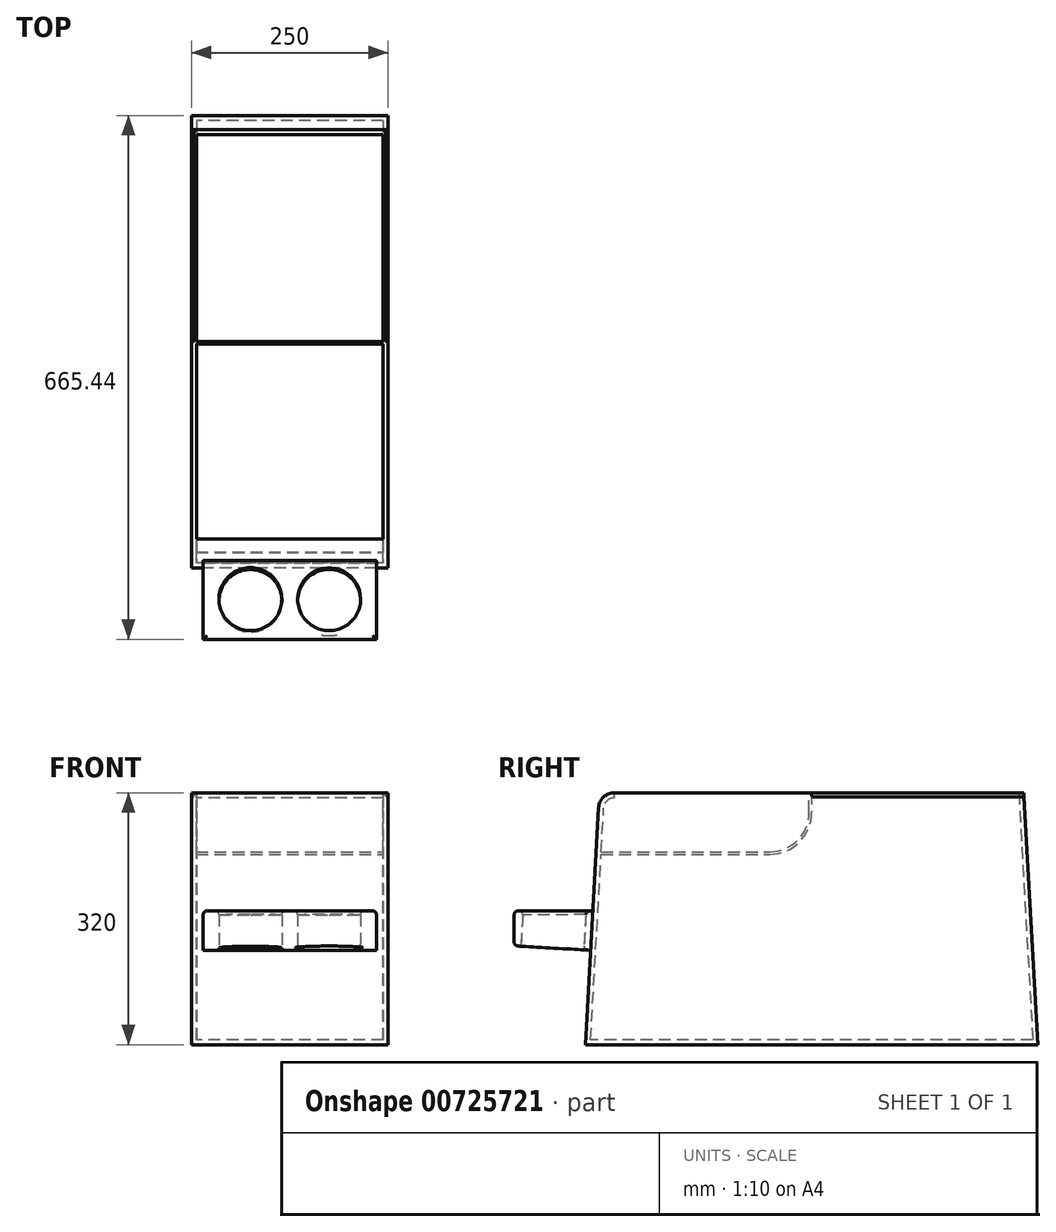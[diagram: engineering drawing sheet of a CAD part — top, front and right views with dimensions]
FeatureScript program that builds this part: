
annotation { "Feature Type Name" : "Feature", "Feature Type Description" : "" }
export const myFeature = defineFeature(function(context is Context, id is Id, definition is map)
    precondition{}
    {
        {
            var Q0;
            Q0=qCreatedBy(makeId("Right.planeOp"),FACE);
            var sketch = newSketch(context, id + "F0", { "sketchPlane" : qUnion([Q0])});
            skLineSegment(sketch, "E0.bottom", {"start": v(287.5, 160) * mm, "end": v(-287.5, 160) * mm});
            skLineSegment(sketch, "E0.top", {"start": v(287.5, -160) * mm, "end": v(-287.5, -160) * mm});
            skLineSegment(sketch, "E0.left", {"start": v(287.5, 160) * mm, "end": v(287.5, -160) * mm});
            skLineSegment(sketch, "E0.right", {"start": v(-287.5, 160) * mm, "end": v(-287.5, -160) * mm});
            skPoint(sketch, "E0.middle", {"position": v(0, 0) * mm});
            skLineSegment(sketch, "E1", {"start": v(-287.5, -160) * mm, "end": v(-270.56, 141.12) * mm});
            skLineSegment(sketch, "E2", {"start": v(-250.6, 160) * mm, "end": v(250.6, 160) * mm});
            skLineSegment(sketch, "E3", {"start": v(269.5, 160) * mm, "end": v(287.5, -160) * mm});
            skPoint(sketch, "E4.visualSharp", {"position": v(-269.5, 160) * mm});
            skArc(sketch, "E4.filletArc", {"start": v(-250.6, 160) * mm, "mid": v(-264.33, 154.53) * mm, "end": v(-270.56, 141.12) * mm});
            skPoint(sketch, "E5.visualSharp", {"position": v(269.5, 160) * mm});
            skSolve(sketch);
        }
        {
            var Q0;
            Q0=makeQuery(id+"F0.imprint","IMPRINT",FACE,{"disambiguationData":[TD([[makeQuery(id+"F0.imprint","IMPRINT",EDGE,{"derivedFrom":sQuery(id+"F0.wireOp",EDGE,"E0.top")}),-1.0]])]});
            extrude(context, id + "F1", {"entities" : qUnion([Q0]), "depth" : 250 * mm, "offsetDistance" : 25 * mm});
        }
        {
            var Q0;
            Q0=makeQuery(id+"F1.opExtrude","SWEPT_FACE",FACE,{"disambiguationData":[OSD([sQuery(id+"F0.wireOp",EDGE,"E0.bottom")])]});
            var Q1;
            Q1=makeQuery(id+"F1.opExtrude","SWEPT_FACE",FACE,{"disambiguationData":[OSD([sQuery(id+"F0.wireOp",EDGE,"E5.filletArc")])]});
            shell(context, id + "F2", {"entities" : qUnion([Q0, Q1]), "thickness" : 6.35 * mm});
        }
        {
            var Q0;
            Q0=makeQuery(id+"F1.opExtrude","CAP_FACE",FACE,{"disambiguationData":[OSD([sQuery(id+"F0.wireOp",EDGE,"E0.bottom"),sQuery(id+"F0.wireOp",EDGE,"E0.top"),sQuery(id+"F0.wireOp",EDGE,"E1"),sQuery(id+"F0.wireOp",EDGE,"E3"),sQuery(id+"F0.wireOp",EDGE,"E4.filletArc")])],"isStart":false});
            var sketch = newSketch(context, id + "F3", { "sketchPlane" : qUnion([Q0])});
            skLineSegment(sketch, "E6", {"start": v(-273.72, 85) * mm, "end": v(-53.17, 85) * mm});
            skLineSegment(sketch, "E7", {"start": v(-273.9, 81.82) * mm, "end": v(-53.17, 81.82) * mm});
            skLineSegment(sketch, "E8", {"start": v(0, 160) * mm, "end": v(0, 135) * mm});
            skLineSegment(sketch, "E9", {"start": v(-53.17, 85) * mm, "end": v(-53.17, 85) * mm});
            skLineSegment(sketch, "E10", {"start": v(-3.17, 135) * mm, "end": v(-3.18, 160) * mm});
            skLineSegment(sketch, "E11", {"start": v(-53.17, 81.82) * mm, "end": v(-53.17, 81.82) * mm});
            skPoint(sketch, "E12.visualSharp", {"position": v(-3.17, 85) * mm});
            skArc(sketch, "E12.filletArc", {"start": v(-53.17, 85) * mm, "mid": v(-17.82, 99.64) * mm, "end": v(-3.17, 135) * mm});
            skPoint(sketch, "E13.visualSharp", {"position": v(0, 81.82) * mm});
            skArc(sketch, "E13.filletArc", {"start": v(-53.17, 81.83) * mm, "mid": v(-15.57, 97.4) * mm, "end": v(0, 135) * mm});
            skSolve(sketch);
        }
        {
            var Q0;
            {var subQ1=sQuery(id+"F3.wireOp",EDGE,"E6");Q0=makeQuery(id+"F3.imprint","IMPRINT",FACE,{"disambiguationData":[TD([[makeQuery(id+"F3.imprint","IMPRINT",EDGE,{"derivedFrom":subQ1}),-1.0]])]});}
            extrude(context, id + "F4", {"entities" : qUnion([Q0]), "operationType" : NewBodyOperationType.ADD, "oppositeDirection" : true, "depth" : 250 * mm, "offsetDistance" : 25 * mm});
        }
        {
            var Q0;
            {var subQ0=sQuery(id+"F0.wireOp",EDGE,"E0.bottom");Q0=makeQuery(id+"F4.boolean.opBoolean","MERGE",FACE,{"derivedFrom":[makeQuery(id+"F1.opExtrude","SWEPT_FACE",FACE,{"disambiguationData":[OSD([subQ0])]}),makeQuery(id+"F4.opExtrude","SWEPT_FACE",FACE,{"disambiguationData":[OSD([subQ0])]})]});}
            var sketch = newSketch(context, id + "F5", { "sketchPlane" : qUnion([Q0])});
            skLineSegment(sketch, "E14.bottom", {"start": v(0, 269.5) * mm, "end": v(3.17, 269.5) * mm});
            skLineSegment(sketch, "E14.top", {"start": v(0, 0) * mm, "end": v(3.18, 0) * mm});
            skLineSegment(sketch, "E14.left", {"start": v(0, 269.5) * mm, "end": v(0, 0) * mm});
            skLineSegment(sketch, "E14.right", {"start": v(3.17, 269.5) * mm, "end": v(3.18, 0) * mm});
            skLineSegment(sketch, "E15.bottom", {"start": v(250, 269.5) * mm, "end": v(246.82, 269.5) * mm});
            skLineSegment(sketch, "E15.top", {"start": v(250, 0) * mm, "end": v(246.83, 0) * mm});
            skLineSegment(sketch, "E15.left", {"start": v(250, 269.5) * mm, "end": v(250, 0) * mm});
            skLineSegment(sketch, "E15.right", {"start": v(246.82, 269.5) * mm, "end": v(246.83, 0) * mm});
            skSolve(sketch);
        }
        {
            var Q0;
            Q0=makeQuery(id+"F5.imprint","IMPRINT",FACE,{"disambiguationData":[TD([[makeQuery(id+"F5.imprint","IMPRINT",EDGE,{"derivedFrom":sQuery(id+"F5.wireOp",EDGE,"E14.bottom")}),1.0]])]});
            var Q1;
            Q1=makeQuery(id+"F5.imprint","IMPRINT",FACE,{"disambiguationData":[TD([[makeQuery(id+"F5.imprint","IMPRINT",EDGE,{"derivedFrom":sQuery(id+"F5.wireOp",EDGE,"E15.bottom")}),1.0]])]});
            extrude(context, id + "F6", {"entities" : qUnion([Q0, Q1]), "operationType" : NewBodyOperationType.REMOVE, "oppositeDirection" : true, "depth" : 5 * mm, "offsetDistance" : 25 * mm});
        }
        {
            var Q0;
            Q0=makeQuery(id+"F6.boolean.opBoolean","COPY",FACE,{"derivedFrom":makeQuery(id+"F6.opExtrude","SWEPT_FACE",FACE,{"disambiguationData":[OSD([sQuery(id+"F5.wireOp",EDGE,"E14.bottom")])]})});
            var Q1;
            Q1=makeQuery(id+"F6.boolean.opBoolean","COPY",FACE,{"derivedFrom":makeQuery(id+"F6.opExtrude","SWEPT_FACE",FACE,{"disambiguationData":[OSD([sQuery(id+"F5.wireOp",EDGE,"E15.bottom")])]})});
            extrude(context, id + "F7", {"entities" : qUnion([Q0, Q1]), "operationType" : NewBodyOperationType.REMOVE, "oppositeDirection" : true, "depth" : 25 * mm, "offsetDistance" : 25 * mm});
        }
        {
            var Q0;
            {var subQ0=sQuery(id+"F5.wireOp",EDGE,"E14.right");var subQ1=sQuery(id+"F5.wireOp",EDGE,"E14.bottom");var subQ2=sQuery(id+"F0.wireOp",EDGE,"E3");var subQ3=sQuery(id+"F0.wireOp",EDGE,"E0.bottom");Q0=makeQuery(id+"F7.boolean.opBoolean","MERGE",EDGE,{"derivedFrom":[makeQuery(id+"F6.boolean.opBoolean","COPY",EDGE,{"derivedFrom":makeQuery(id+"F6.opExtrude","CAP_EDGE",EDGE,{"disambiguationData":[OSD([subQ0])],"isStart":false})})],"fromTools":[makeQuery(id+"F7.opExtrude","SWEPT_EDGE",EDGE,{"disambiguationData":[OSD([subQ3,subQ2,subQ1,subQ0]),TDD([makeQuery(id+"F6.boolean.opBoolean","COPY",VERTEX,{"derivedFrom":makeQuery(id+"F6.opExtrude","CAP_VERTEX",VERTEX,{"disambiguationData":[OSD([subQ3,subQ2,subQ1,subQ0])],"isStart":false})})])]})]});}
            var Q1;
            {var subQ0=sQuery(id+"F5.wireOp",EDGE,"E15.right");var subQ1=sQuery(id+"F5.wireOp",EDGE,"E15.bottom");var subQ2=sQuery(id+"F0.wireOp",EDGE,"E3");var subQ3=sQuery(id+"F0.wireOp",EDGE,"E0.bottom");Q1=makeQuery(id+"F7.boolean.opBoolean","MERGE",EDGE,{"derivedFrom":[makeQuery(id+"F6.boolean.opBoolean","COPY",EDGE,{"derivedFrom":makeQuery(id+"F6.opExtrude","CAP_EDGE",EDGE,{"disambiguationData":[OSD([subQ0])],"isStart":false})})],"fromTools":[makeQuery(id+"F7.opExtrude","SWEPT_EDGE",EDGE,{"disambiguationData":[OSD([subQ3,subQ2,subQ1,subQ0]),TDD([makeQuery(id+"F6.boolean.opBoolean","COPY",VERTEX,{"derivedFrom":makeQuery(id+"F6.opExtrude","CAP_VERTEX",VERTEX,{"disambiguationData":[OSD([subQ3,subQ2,subQ1,subQ0])],"isStart":false})})])]})]});}
            fillet(context, id + "F8", {"entities" : qUnion([Q0, Q1]), "radius" : 1.5 * mm, "tangentPropagation" : true, "allowEdgeOverflow" : false});
        }
        {
            var Q0;
            Q0=makeQuery(id+"F6.boolean.opBoolean","COPY",EDGE,{"derivedFrom":makeQuery(id+"F6.opExtrude","CAP_EDGE",EDGE,{"disambiguationData":[OSD([sQuery(id+"F5.wireOp",EDGE,"E14.top")])],"isStart":false})});
            var Q1;
            Q1=makeQuery(id+"F6.boolean.opBoolean","COPY",EDGE,{"derivedFrom":makeQuery(id+"F6.opExtrude","CAP_EDGE",EDGE,{"disambiguationData":[OSD([sQuery(id+"F5.wireOp",EDGE,"E15.top")])],"isStart":false})});
            fillet(context, id + "F9", {"entities" : qUnion([Q0, Q1]), "radius" : 1.5 * mm, "tangentPropagation" : true, "allowEdgeOverflow" : false});
        }
        {
            var Q0;
            Q0=makeQuery(id+"F1.opExtrude","CAP_FACE",FACE,{"disambiguationData":[OSD([sQuery(id+"F0.wireOp",EDGE,"E0.bottom"),sQuery(id+"F0.wireOp",EDGE,"E0.top"),sQuery(id+"F0.wireOp",EDGE,"E1"),sQuery(id+"F0.wireOp",EDGE,"E3"),sQuery(id+"F0.wireOp",EDGE,"E4.filletArc")])],"isStart":false});
            var sketch = newSketch(context, id + "F10", { "sketchPlane" : qUnion([Q0])});
            skLineSegment(sketch, "E16", {"start": v(-277.94, 10) * mm, "end": v(-280.75, -40) * mm});
            skLineSegment(sketch, "E17", {"start": v(-280.75, -40) * mm, "end": v(-377.94, -34.53) * mm});
            skLineSegment(sketch, "E18", {"start": v(-377.94, -34.53) * mm, "end": v(-377.94, 10) * mm});
            skLineSegment(sketch, "E19", {"start": v(-377.94, 10) * mm, "end": v(-277.94, 10) * mm});
            skSolve(sketch);
        }
        {
            var Q0;
            Q0=makeQuery(id+"F10.imprint","IMPRINT",FACE,{"disambiguationData":[TD([[makeQuery(id+"F10.imprint","IMPRINT",EDGE,{"derivedFrom":sQuery(id+"F10.wireOp",EDGE,"E16")}),1.0]])]});
            extrude(context, id + "F11", {"entities" : qUnion([Q0]), "operationType" : NewBodyOperationType.ADD, "oppositeDirection" : true, "depth" : 250 * mm, "offsetDistance" : 25 * mm});
        }
        {
            var Q0;
            Q0=makeQuery(id+"F11.opExtrude","SWEPT_FACE",FACE,{"disambiguationData":[OSD([sQuery(id+"F10.wireOp",EDGE,"E17")])]});
            var sketch = newSketch(context, id + "F12", { "sketchPlane" : qUnion([Q0])});
            skLineSegment(sketch, "E20.bottom", {"start": v(0, 278.06) * mm, "end": v(15, 278.06) * mm});
            skLineSegment(sketch, "E20.top", {"start": v(0, 400.96) * mm, "end": v(15, 400.96) * mm});
            skLineSegment(sketch, "E20.left", {"start": v(0, 278.06) * mm, "end": v(0, 400.96) * mm});
            skLineSegment(sketch, "E20.right", {"start": v(15, 278.06) * mm, "end": v(15, 400.96) * mm});
            skLineSegment(sketch, "E21.bottom", {"start": v(250, 278.06) * mm, "end": v(235, 278.06) * mm});
            skLineSegment(sketch, "E21.top", {"start": v(250, 394.07) * mm, "end": v(235, 394.07) * mm});
            skLineSegment(sketch, "E21.left", {"start": v(250, 278.06) * mm, "end": v(250, 394.07) * mm});
            skLineSegment(sketch, "E21.right", {"start": v(235, 278.06) * mm, "end": v(235, 394.07) * mm});
            skSolve(sketch);
        }
        {
            var Q0;
            {var subQ0=sQuery(id+"F12.wireOp",EDGE,"E21.bottom");Q0=makeQuery(id+"F12.imprint","IMPRINT",FACE,{"disambiguationData":[TD([[makeQuery(id+"F12.imprint","IMPRINT",EDGE,{"derivedFrom":subQ0}),1.0]])]});}
            var Q1;
            {var subQ0=sQuery(id+"F12.wireOp",EDGE,"E20.top");Q1=makeQuery(id+"F12.imprint","IMPRINT",FACE,{"disambiguationData":[TD([[makeQuery(id+"F12.imprint","IMPRINT",EDGE,{"derivedFrom":subQ0}),-1.0]])]});}
            var Q2;
            {var subQ0=sQuery(id+"F12.wireOp",EDGE,"E20.bottom");Q2=makeQuery(id+"F12.imprint","IMPRINT",FACE,{"disambiguationData":[TD([[makeQuery(id+"F12.imprint","IMPRINT",EDGE,{"derivedFrom":subQ0}),1.0]])]});}
            var Q3;
            {var subQ0=sQuery(id+"F12.wireOp",EDGE,"E21.top");Q3=makeQuery(id+"F12.imprint","IMPRINT",FACE,{"disambiguationData":[TD([[makeQuery(id+"F12.imprint","IMPRINT",EDGE,{"derivedFrom":subQ0}),1.0]])]});}
            extrude(context, id + "F13", {"entities" : qUnion([Q0, Q1, Q2, Q3]), "operationType" : NewBodyOperationType.REMOVE, "oppositeDirection" : true, "depth" : 50.1 * mm, "offsetDistance" : 25 * mm});
        }
        {
            var Q0;
            Q0=makeQuery(id+"F11.opExtrude","SWEPT_FACE",FACE,{"disambiguationData":[OSD([sQuery(id+"F10.wireOp",EDGE,"E17")])]});
            var sketch = newSketch(context, id + "F14", { "sketchPlane" : qUnion([Q0])});
            skLineSegment(sketch, "E22", {"start": v(235, 326.73) * mm, "end": v(15, 326.73) * mm, "construction": true});
            skCircle(sketch, "E23", {"center": v(175, 326.73) * mm, "radius": 40 * mm});
            skCircle(sketch, "E24", {"center": v(75, 326.73) * mm, "radius": 40 * mm});
            skSolve(sketch);
        }
        {
            var Q0;
            Q0=makeQuery(id+"F14.imprint","IMPRINT",FACE,{"disambiguationData":[TD([[makeQuery(id+"F14.imprint","IMPRINT",EDGE,{"derivedFrom":sQuery(id+"F14.wireOp",EDGE,"E23")}),1.0]])]});
            var Q1;
            Q1=makeQuery(id+"F14.imprint","IMPRINT",FACE,{"disambiguationData":[TD([[makeQuery(id+"F14.imprint","IMPRINT",EDGE,{"derivedFrom":sQuery(id+"F14.wireOp",EDGE,"E24")}),1.0]])]});
            extrude(context, id + "F15", {"entities" : qUnion([Q0, Q1]), "operationType" : NewBodyOperationType.REMOVE, "oppositeDirection" : true, "depth" : 50.1 * mm, "offsetDistance" : 25 * mm});
        }
        {
            var Q0;
            Q0=makeQuery(id+"F11.opExtrude","SWEPT_EDGE",EDGE,{"disambiguationData":[OSD([sQuery(id+"F10.wireOp",EDGE,"E17"),sQuery(id+"F10.wireOp",EDGE,"E18")])]});
            var Q1;
            Q1=makeQuery(id+"F13.boolean.opBoolean","COPY",EDGE,{"derivedFrom":makeQuery(id+"F13.opExtrude","CAP_EDGE",EDGE,{"disambiguationData":[OSD([sQuery(id+"F12.wireOp",EDGE,"E20.right")])],"isStart":true})});
            var Q2;
            Q2=makeQuery(id+"F13.boolean.opBoolean","INTERSECT",EDGE,{"derivedFrom":[makeQuery(id+"F11.opExtrude","SWEPT_FACE",FACE,{"disambiguationData":[OSD([sQuery(id+"F10.wireOp",EDGE,"E19")])]}),makeQuery(id+"F13.opExtrude","SWEPT_FACE",FACE,{"disambiguationData":[OSD([sQuery(id+"F12.wireOp",EDGE,"E20.right")])]})]});
            var Q3;
            Q3=makeQuery(id+"F11.opExtrude","SWEPT_EDGE",EDGE,{"disambiguationData":[OSD([sQuery(id+"F10.wireOp",EDGE,"E18"),sQuery(id+"F10.wireOp",EDGE,"E19")])]});
            var Q4;
            Q4=makeQuery(id+"F13.boolean.opBoolean","COPY",EDGE,{"derivedFrom":makeQuery(id+"F13.opExtrude","CAP_EDGE",EDGE,{"disambiguationData":[OSD([sQuery(id+"F12.wireOp",EDGE,"E21.right")])],"isStart":true})});
            var Q5;
            Q5=makeQuery(id+"F13.boolean.opBoolean","INTERSECT",EDGE,{"derivedFrom":[makeQuery(id+"F11.opExtrude","SWEPT_FACE",FACE,{"disambiguationData":[OSD([sQuery(id+"F10.wireOp",EDGE,"E19")])]}),makeQuery(id+"F13.opExtrude","SWEPT_FACE",FACE,{"disambiguationData":[OSD([sQuery(id+"F12.wireOp",EDGE,"E21.right")])]})]});
            var Q6;
            Q6=makeQuery(id+"F15.boolean.opBoolean","COPY",FACE,{"derivedFrom":makeQuery(id+"F15.opExtrude","SWEPT_FACE",FACE,{"disambiguationData":[OSD([sQuery(id+"F14.wireOp",EDGE,"E23")])]})});
            var Q7;
            Q7=makeQuery(id+"F15.boolean.opBoolean","COPY",EDGE,{"derivedFrom":makeQuery(id+"F15.opExtrude","CAP_EDGE",EDGE,{"disambiguationData":[OSD([sQuery(id+"F14.wireOp",EDGE,"E24")])],"isStart":true})});
            var Q8;
            Q8=makeQuery(id+"F15.boolean.opBoolean","INTERSECT",EDGE,{"derivedFrom":[makeQuery(id+"F11.opExtrude","SWEPT_FACE",FACE,{"disambiguationData":[OSD([sQuery(id+"F10.wireOp",EDGE,"E19")])]}),makeQuery(id+"F15.opExtrude","SWEPT_FACE",FACE,{"disambiguationData":[OSD([sQuery(id+"F14.wireOp",EDGE,"E24")])]})]});
            fillet(context, id + "F16", {"entities" : qUnion([Q0, Q1, Q2, Q3, Q4, Q5, Q6, Q7, Q8]), "radius" : 5 * mm, "tangentPropagation" : true, "allowEdgeOverflow" : false});
        }
    });
